# Revit family: 2059381 Sylvania Lighting Fixture ASCENT 150 II SQ 1100 3K DALI
name_source: partatom
category: Lighting Fixtures
revit_build: Autodesk Revit 2016 (Build: 20150220_1215(x64)
units: mm (PartAtom-declared; Revit-internal decimal feet)

## family parameters
Cut with Voids When Loaded = No
Host = Face
Light Source = Yes
OmniClass Number = 23.80.70.11.17
OmniClass Title = Specialized Lighting by Location or Use
Part Type = Normal
Room Calculation Point = No
Round Connector Dimension = Use Diameter
Shared = No

## types (1)
- 2059381 ASCENT 150 II SQ 1100 3K DALI
    Apparent Load = 10 VA
    Assembly Code = D5020200
    AssetType = Fixed
    Color Filter = 16777215
    Default Elevation = 0 mm  [stored 0 ft]
    Description = The ASCENT 150 II SQ 1100 3K DALI  is a high efficient downlight luminaire with luminous flux: 1163lm, luminaire efficacy: 117lm/W, Colour rendering index Ra >80, Colour temperature: 3000K Warm white, Average life rated at 50,000Hrs, Class II, Protection rating IP44/IK02, Cut out dimensions: 175mm, Weight: 1.7kg
    Dimming Lamp Color Temperature Shift = <None>
    DocumentationLiterature = http://www.sylvania-lighting.com
    DurationUnit = hours
    ElectricShockClassification = Class II
    Emit Shape Visible in Rendering = No
    Emit from Rectangle Length = 154 mm
    Emit from Rectangle Width = 154 mm
    ExpectedLife = 50000
    Height_SYL = 158 mm
    IfcExportAs = IfcLightFixtureType
    IfcExportType = IfcLightFixtureType
    ImpactProtectionIndex = IK02
    IngressProtection = IP44
    Keynote = 16500
    Lamp = LED
    LampColourRenderingIndex = 80
    LampColourTemperature = 3000 K
    LampNominalLuminous = 1163 lm
    LampsType = LED
    Length_SYL = 188 mm  [stored 0.616798 ft]
    LightOutputRatio = 100
    LuminousEfficacy = 117 lm/W
    Manufacturer = Feilo Sylvania
    ManufacturerName = Feilo Sylvania
    Material = aluminium housing
    Material_1_SYL = Stainless Steel_Acc_Sylvania_White
    Material_2_SYL = Aluminium_Reflector_Sylvania
    Material_3_SYL = Stainless Steel_Body_Sylvania_Black
    Material_4_SYL = LED_Sylvania
    Model = ASCENT 150 II SQ 1100 3K DALI
    ModelNumber = 2059381
    ModelReference = ASCENT 150 II SQ 1100 3K DALI
    Name = ASCENT 150 II SQ 1100 3K DALI
    NominalHeight = 158 mm
    NominalLength = 0 mm  [stored 0 ft]
    NominalWidth = 0 mm  [stored 0 ft]
    Photometric Web File = 2059381.ies
    PowerConsumption = 10 W
    PowerFactor = 0
    Tilt Angle = -90.00°
    TypeName = ASCENT 150 II SQ 1100 3K DALI
    URL = http://www.sylvania-lighting.com
    Voltage = 0 V
    Weight = 1.7 kg
    Width_SYL = 188 mm  [stored 0.616798 ft]

note: [stored X ft] marks values corroborated as IEEE doubles in the binary element streams (Revit-internal decimal feet)

## geometry (parser evidence)
native form markers: Sweep x2
no freeform markers — native parametric forms only
